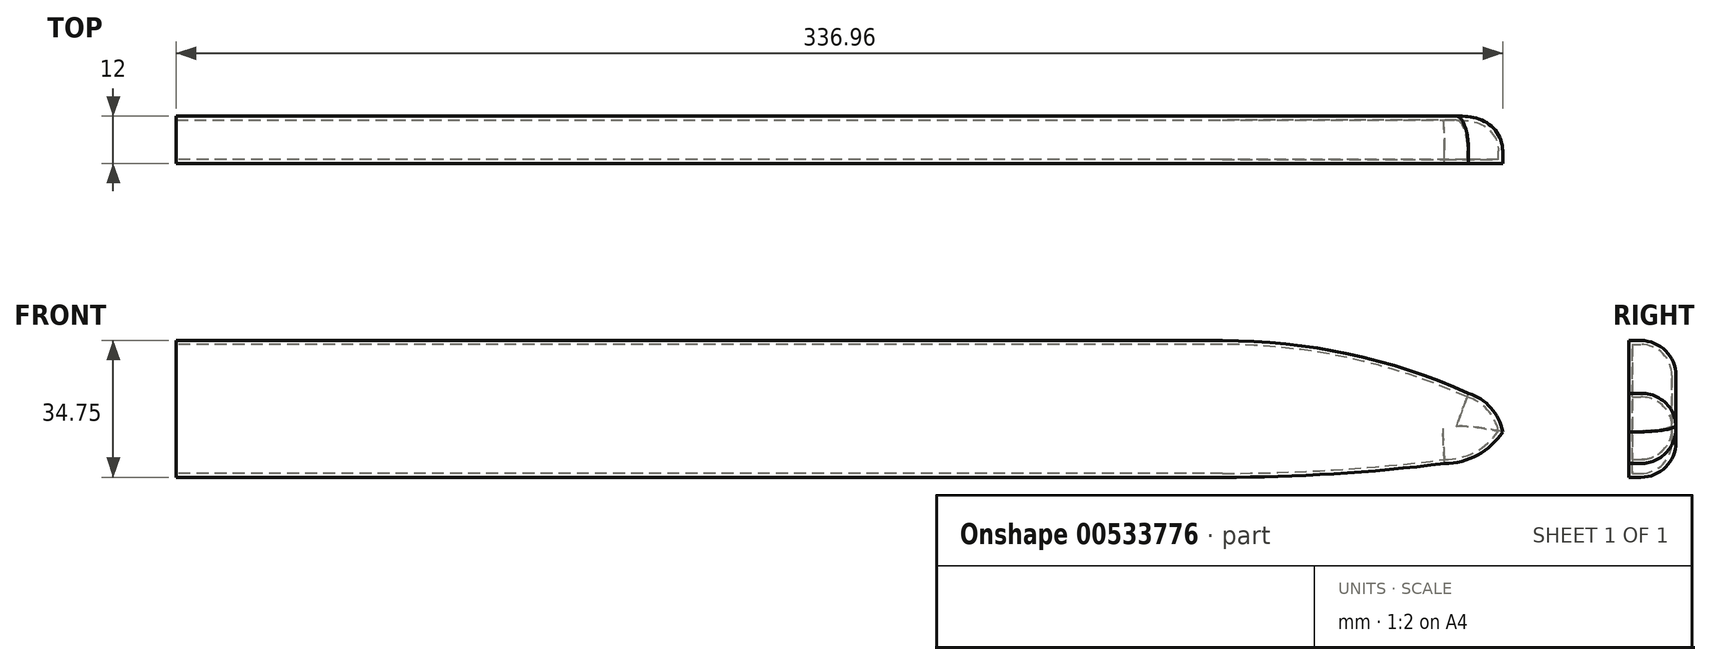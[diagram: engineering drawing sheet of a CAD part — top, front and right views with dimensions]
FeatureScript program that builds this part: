
annotation { "Feature Type Name" : "Feature", "Feature Type Description" : "" }
export const myFeature = defineFeature(function(context is Context, id is Id, definition is map)
    precondition{}
    {
        {
            var Q0;
            Q0=qCreatedBy(makeId("Front.planeOp"),FACE);
            var sketch = newSketch(context, id + "F0", { "sketchPlane" : qUnion([Q0])});
            skLineSegment(sketch, "E0.bottom", {"start": v(67.6, 31.79) * mm, "end": v(-198.16, 31.79) * mm});
            skLineSegment(sketch, "E0.top", {"start": v(67.6, -2.96) * mm, "end": v(-198.16, -2.96) * mm});
            skLineSegment(sketch, "E0.left", {"start": v(67.6, 31.79) * mm, "end": v(67.6, -2.96) * mm});
            skLineSegment(sketch, "E0.right", {"start": v(-198.16, 31.79) * mm, "end": v(-198.16, -2.96) * mm});
            skArc(sketch, "E1", {"start": v(130.14, 18.4) * mm, "mid": v(99.57, 28.4) * mm, "end": v(67.6, 31.79) * mm});
            skArc(sketch, "E2", {"start": v(67.6, -2.96) * mm, "mid": v(95.88, -2.09) * mm, "end": v(124.05, 0.55) * mm});
            skArc(sketch, "E3", {"start": v(124.05, 0.55) * mm, "mid": v(132.45, 2.7) * mm, "end": v(138.8, 8.61) * mm});
            skArc(sketch, "E4", {"start": v(138.8, 8.61) * mm, "mid": v(135.81, 14.7) * mm, "end": v(130.14, 18.4) * mm});
            skSolve(sketch);
        }
        {
            var Q0;
            Q0 = qSketchRegion(id + "F0", true);
            extrude(context, id + "F1", {"entities" : qUnion([Q0]), "depth" : 12 * mm, "offsetDistance" : 25 * mm});
        }
        {
            var Q0;
            Q0=makeQuery(id+"F1.opExtrude","CAP_EDGE",EDGE,{"disambiguationData":[OSD([sQuery(id+"F0.wireOp",EDGE,"E0.bottom")])],"isStart":true});
            var Q1;
            Q1=makeQuery(id+"F1.opExtrude","CAP_EDGE",EDGE,{"disambiguationData":[OSD([sQuery(id+"F0.wireOp",EDGE,"E0.top")])],"isStart":true});
            var Q2;
            Q2=makeQuery(id+"F1.opExtrude","CAP_EDGE",EDGE,{"disambiguationData":[OSD([sQuery(id+"F0.wireOp",EDGE,"E3")])],"isStart":true});
            var Q3;
            Q3=makeQuery(id+"F1.opExtrude","CAP_EDGE",EDGE,{"disambiguationData":[OSD([sQuery(id+"F0.wireOp",EDGE,"E1")])],"isStart":true});
            var Q4;
            Q4=makeQuery(id+"F1.opExtrude","CAP_EDGE",EDGE,{"disambiguationData":[OSD([sQuery(id+"F0.wireOp",EDGE,"E4")])],"isStart":true});
            fillet(context, id + "F2", {"entities" : qUnion([Q0, Q1, Q2, Q3, Q4]), "radius" : 8.9 * mm, "tangentPropagation" : true, "allowEdgeOverflow" : false});
        }
        {
            var Q0;
            Q0=makeQuery(id+"F1.opExtrude","SWEPT_FACE",FACE,{"disambiguationData":[OSD([sQuery(id+"F0.wireOp",EDGE,"E0.right")])]});
            shell(context, id + "F3", {"entities" : qUnion([Q0]), "thickness" : 1 * mm});
        }
    });
